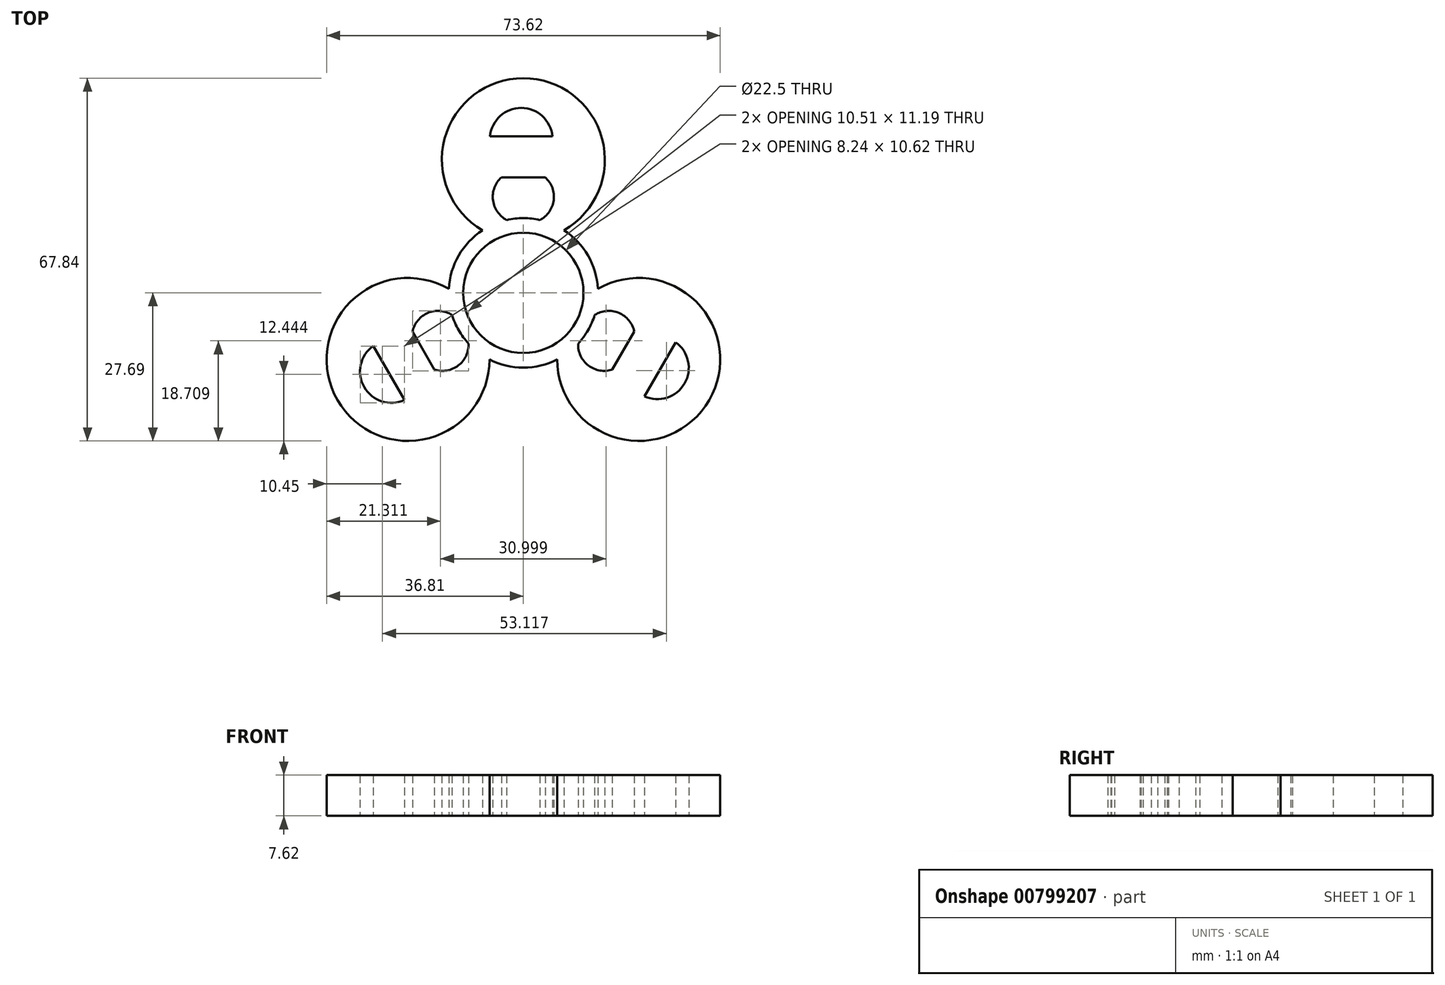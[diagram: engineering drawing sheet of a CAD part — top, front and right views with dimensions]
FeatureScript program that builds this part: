
annotation { "Feature Type Name" : "Feature", "Feature Type Description" : "" }
export const myFeature = defineFeature(function(context is Context, id is Id, definition is map)
    precondition{}
    {
        {
            var Q0;
            Q0=qCreatedBy(makeId("Top.planeOp"),FACE);
            var sketch = newSketch(context, id + "F0", { "sketchPlane" : qUnion([Q0])});
            skCircle(sketch, "E0", {"center": v(0, 0) * mm, "radius": 11.25 * mm});
            skCircle(sketch, "E1", {"center": v(0, 0) * mm, "radius": 13.97 * mm});
            skArc(sketch, "E2", {"start": v(7.62, 11.7) * mm, "mid": v(0, 40.15) * mm, "end": v(-7.62, 11.7) * mm});
            skLineSegment(sketch, "E3", {"start": v(-6.23, 29.28) * mm, "end": v(5.43, 29.28) * mm});
            skArc(sketch, "E4", {"start": v(5.43, 29.28) * mm, "mid": v(-0.4, 34.6) * mm, "end": v(-6.23, 29.28) * mm});
            skArc(sketch, "E5", {"start": v(-4.1, 21.6) * mm, "mid": v(-5.68, 17.34) * mm, "end": v(-3.1, 13.62) * mm});
            skLineSegment(sketch, "E6", {"start": v(-4.1, 21.6) * mm, "end": v(-0.81, 21.6) * mm});
            skArc(sketch, "E7.MirrorCS", {"start": v(4.1, 21.6) * mm, "mid": v(5.68, 17.34) * mm, "end": v(3.1, 13.62) * mm});
            skLineSegment(sketch, "E8.MirrorCS", {"start": v(4.1, 21.6) * mm, "end": v(0.81, 21.6) * mm});
            skArc(sketch, "E9.1.0", {"start": v(-16.65, -14.35) * mm, "mid": v(-12.18, -13.6) * mm, "end": v(-10.25, -9.5) * mm});
            skArc(sketch, "E9.1.1", {"start": v(-28.07, -9.93) * mm, "mid": v(-29.76, -17.64) * mm, "end": v(-22.24, -20.03) * mm});
            skArc(sketch, "E9.1.2", {"start": v(-13.95, 0.74) * mm, "mid": v(-34.77, -20.07) * mm, "end": v(-6.33, -12.45) * mm});
            skArc(sketch, "E9.1.3", {"start": v(-20.75, -7.24) * mm, "mid": v(-17.86, -3.75) * mm, "end": v(-13.35, -4.13) * mm});
            skLineSegment(sketch, "E9.1.4", {"start": v(-22.24, -20.03) * mm, "end": v(-28.07, -9.93) * mm});
            skLineSegment(sketch, "E9.1.5", {"start": v(-16.65, -14.35) * mm, "end": v(-18.3, -11.5) * mm});
            skLineSegment(sketch, "E9.1.6", {"start": v(-20.75, -7.24) * mm, "end": v(-19.1, -10.1) * mm});
            skArc(sketch, "E9.2.0", {"start": v(20.75, -7.24) * mm, "mid": v(17.86, -3.75) * mm, "end": v(13.35, -4.13) * mm});
            skArc(sketch, "E9.2.1", {"start": v(22.64, -19.34) * mm, "mid": v(30.16, -16.95) * mm, "end": v(28.47, -9.25) * mm});
            skArc(sketch, "E9.2.2", {"start": v(6.33, -12.45) * mm, "mid": v(34.77, -20.07) * mm, "end": v(13.95, 0.74) * mm});
            skArc(sketch, "E9.2.3", {"start": v(16.65, -14.35) * mm, "mid": v(12.18, -13.6) * mm, "end": v(10.25, -9.5) * mm});
            skLineSegment(sketch, "E9.2.4", {"start": v(28.47, -9.25) * mm, "end": v(22.64, -19.34) * mm});
            skLineSegment(sketch, "E9.2.5", {"start": v(20.75, -7.24) * mm, "end": v(19.1, -10.1) * mm});
            skLineSegment(sketch, "E9.2.6", {"start": v(16.65, -14.35) * mm, "end": v(18.3, -11.5) * mm});
            skLineSegment(sketch, "E10", {"start": v(-20.75, -7.24) * mm, "end": v(-16.65, -14.35) * mm});
            skLineSegment(sketch, "E11", {"start": v(-4.1, 21.6) * mm, "end": v(4.1, 21.6) * mm});
            skLineSegment(sketch, "E12", {"start": v(16.65, -14.35) * mm, "end": v(20.75, -7.24) * mm});
            skArc(sketch, "E13", {"start": v(-4.1, 21.6) * mm, "mid": v(-5.59, 17.36) * mm, "end": v(-3.1, 13.62) * mm});
            skArc(sketch, "E14", {"start": v(3.1, 13.62) * mm, "mid": v(5.65, 17.35) * mm, "end": v(4.1, 21.6) * mm});
            skArc(sketch, "E15.1.3", {"start": v(-16.65, -14.35) * mm, "mid": v(-12.24, -13.52) * mm, "end": v(-10.25, -9.5) * mm});
            skLineSegment(sketch, "E15.1.4", {"start": v(-16.65, -14.35) * mm, "end": v(-20.75, -7.24) * mm});
            skArc(sketch, "E15.1.5", {"start": v(-13.35, -4.13) * mm, "mid": v(-17.85, -3.78) * mm, "end": v(-20.75, -7.24) * mm});
            skArc(sketch, "E15.2.3", {"start": v(20.75, -7.24) * mm, "mid": v(17.82, -3.84) * mm, "end": v(13.35, -4.13) * mm});
            skLineSegment(sketch, "E15.2.4", {"start": v(20.75, -7.24) * mm, "end": v(16.65, -14.35) * mm});
            skArc(sketch, "E15.2.5", {"start": v(10.25, -9.5) * mm, "mid": v(12.2, -13.57) * mm, "end": v(16.65, -14.35) * mm});
            skSolve(sketch);
        }
        {
            var Q0;
            Q0=makeQuery(id+"F0.imprint","IMPRINT",FACE,{"disambiguationData":[TD([[makeQuery(id+"F0.imprint","IMPRINT",EDGE,{"derivedFrom":sQuery(id+"F0.wireOp",EDGE,"E9.1.1")}),-1.0]])]});
            var Q1;
            Q1=makeQuery(id+"F0.imprint","IMPRINT",FACE,{"disambiguationData":[TD([[makeQuery(id+"F0.imprint","IMPRINT",EDGE,{"derivedFrom":sQuery(id+"F0.wireOp",EDGE,"E9.2.1")}),-1.0]])]});
            var Q2;
            {var subQ0=sQuery(id+"F0.wireOp",EDGE,"E2");Q2=makeQuery(id+"F0.imprint","IMPRINT",FACE,{"disambiguationData":[TD([[makeQuery(id+"F0.imprint","IMPRINT",EDGE,{"derivedFrom":subQ0}),1.0]])]});}
            var Q3;
            Q3=makeQuery(id+"F0.imprint","IMPRINT",FACE,{"disambiguationData":[TD([[makeQuery(id+"F0.imprint","IMPRINT",EDGE,{"derivedFrom":sQuery(id+"F0.wireOp",EDGE,"E0")}),-1.0]])]});
            extrude(context, id + "F1", {"entities" : qUnion([Q0, Q1, Q2, Q3]), "depth" : 7.62 * mm, "offsetDistance" : 25.4 * mm});
        }
    });
